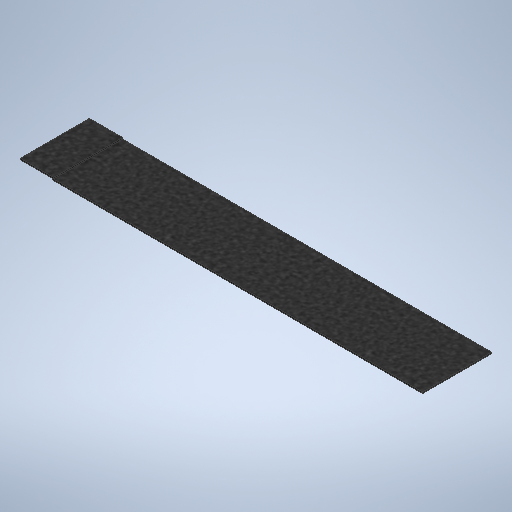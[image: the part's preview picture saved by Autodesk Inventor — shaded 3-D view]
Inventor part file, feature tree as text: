
AUTODESK INVENTOR PART (.ipt)
format: ipt  version: 2025.1 (Build 291241020, 241B)  size: 282,624 bytes
history: native  units: in
note: dims shown in document units (in); Inventor stores cm internally (conversion verified against a paired STEP export)
features: extrude x1, sketch x1
ambient origin geometry x8: Origin, YZ Plane, XZ Plane, XY Plane, X Axis, Y Axis, Z Axis, Center Point
bodies: Body1 (feature_tree)
feature tree (2):
  extrude  "Extrusion2"  Depth=0.125in
  sketch  "Sketch1"  dims[d0=3.0in d1=0.125in d2=0.125in d3=0.125in d4=0.125in d8=6.5in d9=0.0in d10=34.875in]
